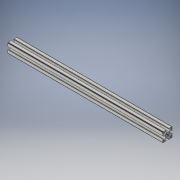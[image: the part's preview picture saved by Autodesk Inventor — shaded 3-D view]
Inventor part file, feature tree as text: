
AUTODESK INVENTOR PART (.ipt)
format: ipt  version: 2016 (Build 200138000, 138)  size: 1,109,504 bytes
history: native  units: in
note: dims shown in document units (in); Inventor stores cm internally (conversion verified against a paired STEP export)
features: extrude x1, sketch x1
ambient origin geometry x8: Origin, YZ Plane, XZ Plane, XY Plane, X Axis, Y Axis, Z Axis, Center Point
bodies: Solid1 (feature_tree)
feature tree (2):
  extrude  "Extrusion1"  [1 undecoded]
  sketch  "Sketch1"  dims[d0=18.937in d1=0.0in]
note: 1 required parameter value undecoded (feature->parameter linkage not recoverable at this tier; creation-order binding heuristic only, values carry confidence <= 0.55)
